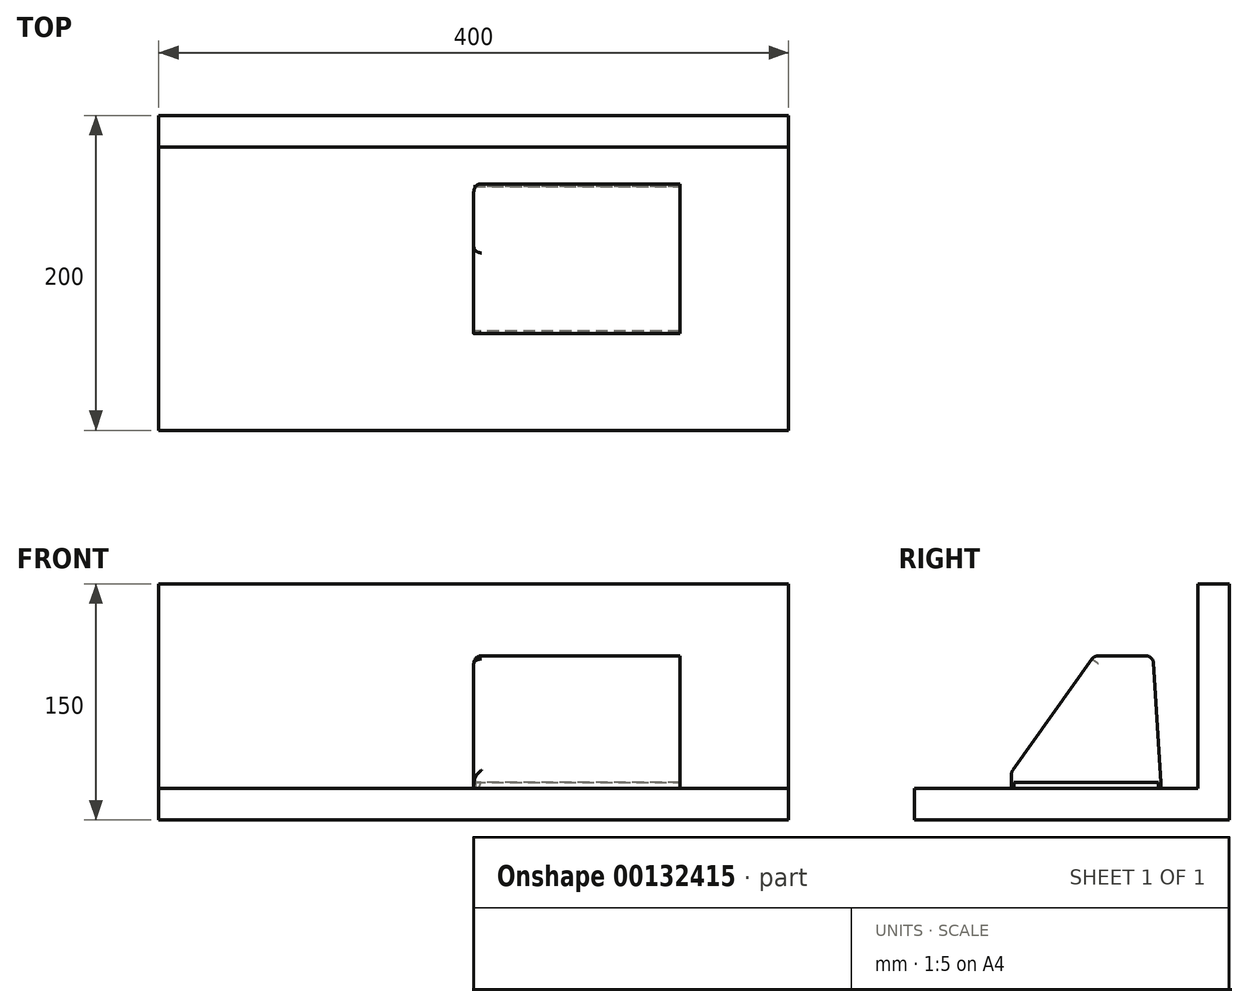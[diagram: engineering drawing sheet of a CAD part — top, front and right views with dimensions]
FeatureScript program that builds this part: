
annotation { "Feature Type Name" : "Feature", "Feature Type Description" : "" }
export const myFeature = defineFeature(function(context is Context, id is Id, definition is map)
    precondition{}
    {
        {
            var Q0;
            Q0=qCreatedBy(makeId("Right.planeOp"),FACE);
            var sketch = newSketch(context, id + "F0", { "sketchPlane" : qUnion([Q0])});
            skLineSegment(sketch, "E0", {"start": v(-180, 0) * mm, "end": v(0, 0) * mm});
            skLineSegment(sketch, "E1", {"start": v(0, 0) * mm, "end": v(0, 130) * mm});
            skLineSegment(sketch, "E2", {"start": v(0, 130) * mm, "end": v(20, 130) * mm});
            skLineSegment(sketch, "E3", {"start": v(20, 130) * mm, "end": v(20, -20) * mm});
            skLineSegment(sketch, "E4", {"start": v(20, -20) * mm, "end": v(-180, -20) * mm});
            skLineSegment(sketch, "E5", {"start": v(-180, -20) * mm, "end": v(-180, 0) * mm});
            skSolve(sketch);
        }
        {
            var Q0;
            Q0 = qSketchRegion(id + "F0", true);
            extrude(context, id + "F1", {"entities" : qUnion([Q0]), "endBound" : BoundingType.SYMMETRIC, "depth" : 400 * mm});
        }
        {
            var Q0;
            Q0=makeQuery(id+"F1.opExtrude","SWEPT_FACE",FACE,{"disambiguationData":[OSD([sQuery(id+"F0.wireOp",EDGE,"E0")])]});
            var sketch = newSketch(context, id + "F2", { "sketchPlane" : qUnion([Q0])});
            skLineSegment(sketch, "E6.bottom", {"start": v(0, -117) * mm, "end": v(131, -117) * mm});
            skLineSegment(sketch, "E6.top", {"start": v(0, -25) * mm, "end": v(131, -25) * mm});
            skLineSegment(sketch, "E6.left", {"start": v(0, -117) * mm, "end": v(0, -25) * mm});
            skLineSegment(sketch, "E6.right", {"start": v(131, -117) * mm, "end": v(131, -25) * mm});
            skSolve(sketch);
        }
        {
            var Q0;
            Q0 = qSketchRegion(id + "F2", true);
            extrude(context, id + "F3", {"entities" : qUnion([Q0]), "depth" : 4 * mm});
        }
        {
            var Q0;
            Q0=qCreatedBy(makeId("Right.planeOp"),FACE);
            var sketch = newSketch(context, id + "F4", { "sketchPlane" : qUnion([Q0])});
            skLineSegment(sketch, "E7", {"start": v(-65, 82.84) * mm, "end": v(-30, 82.84) * mm});
            skLineSegment(sketch, "E8", {"start": v(-25, 4) * mm, "end": v(-25, 0) * mm});
            skLineSegment(sketch, "E9.0", {"start": v(-23.5, 4.05) * mm, "end": v(-23.5, 0) * mm});
            skLineSegment(sketch, "E9.1", {"start": v(-118.5, 0) * mm, "end": v(-118.5, 10.48) * mm});
            skLineSegment(sketch, "E9.2", {"start": v(-118.5, 10.48) * mm, "end": v(-65.77, 84.34) * mm});
            skLineSegment(sketch, "E9.3", {"start": v(-65.77, 84.34) * mm, "end": v(-28.6, 84.34) * mm});
            skLineSegment(sketch, "E9.4", {"start": v(-23.5, 4.05) * mm, "end": v(-28.6, 84.34) * mm});
            skLineSegment(sketch, "E10", {"start": v(-117, 4) * mm, "end": v(-25, 4) * mm});
            skLineSegment(sketch, "E11", {"start": v(-117, 4) * mm, "end": v(-117, 0) * mm});
            skLineSegment(sketch, "E12", {"start": v(-118.5, 0) * mm, "end": v(-117, 0) * mm});
            skLineSegment(sketch, "E13", {"start": v(-25, 0) * mm, "end": v(-23.5, 0) * mm});
            skSolve(sketch);
        }
        {
            var Q0;
            Q0 = qSketchRegion(id + "F4", true);
            var Q1;
            Q1=makeQuery(id+"F3.opExtrude","SWEPT_FACE",FACE,{"disambiguationData":[OSD([sQuery(id+"F2.wireOp",EDGE,"E6.right")])]});
            extrude(context, id + "F5", {"entities" : qUnion([Q0]), "endBound" : BoundingType.UP_TO_SURFACE, "endBoundEntityFace" : qUnion([Q1]), "depth" : 124 * mm});
        }
        {
            var Q0;
            Q0=makeQuery(id+"F5.opExtrude","TWEAK_EDGE",EDGE,{"derivedFrom":[makeQuery(id+"F3.opExtrude","SWEPT_FACE",FACE,{"disambiguationData":[OSD([sQuery(id+"F2.wireOp",EDGE,"E6.right")])]}),makeQuery(id+"F4.imprint","IMPRINT",EDGE,{"derivedFrom":sQuery(id+"F4.wireOp",EDGE,"E9.2")})]});
            var Q1;
            Q1=makeQuery(id+"F5.opExtrude","CAP_EDGE",EDGE,{"disambiguationData":[OSD([sQuery(id+"F4.wireOp",EDGE,"E9.2")])],"isStart":true});
            var Q2;
            Q2=makeQuery(id+"F5.opExtrude","SWEPT_EDGE",EDGE,{"disambiguationData":[OSD([sQuery(id+"F4.wireOp",EDGE,"E9.1"),sQuery(id+"F4.wireOp",EDGE,"E9.2")])]});
            var Q3;
            Q3=makeQuery(id+"F5.opExtrude","SWEPT_EDGE",EDGE,{"disambiguationData":[OSD([sQuery(id+"F4.wireOp",EDGE,"E9.2"),sQuery(id+"F4.wireOp",EDGE,"E9.3")])]});
            fillet(context, id + "F6", {"entities" : qUnion([Q0, Q1, Q2, Q3]), "radius" : 5 * mm, "tangentPropagation" : true, "allowEdgeOverflow" : false});
        }
        {
            var Q0;
            Q0=makeQuery(id+"F5.opExtrude","TWEAK_EDGE",EDGE,{"derivedFrom":[makeQuery(id+"F3.opExtrude","SWEPT_FACE",FACE,{"disambiguationData":[OSD([sQuery(id+"F2.wireOp",EDGE,"E6.right")])]}),makeQuery(id+"F4.imprint","IMPRINT",EDGE,{"derivedFrom":sQuery(id+"F4.wireOp",EDGE,"E9.3")})]});
            var Q1;
            Q1=makeQuery(id+"F5.opExtrude","SWEPT_EDGE",EDGE,{"disambiguationData":[OSD([sQuery(id+"F4.wireOp",EDGE,"E9.3"),sQuery(id+"F4.wireOp",EDGE,"E9.4")])]});
            var Q2;
            Q2=makeQuery(id+"F5.opExtrude","CAP_EDGE",EDGE,{"disambiguationData":[OSD([sQuery(id+"F4.wireOp",EDGE,"E9.3")])],"isStart":true});
            var Q3;
            Q3=makeQuery(id+"F5.opExtrude","TWEAK_EDGE",EDGE,{"derivedFrom":[makeQuery(id+"F3.opExtrude","SWEPT_FACE",FACE,{"disambiguationData":[OSD([sQuery(id+"F2.wireOp",EDGE,"E6.right")])]}),makeQuery(id+"F4.imprint","IMPRINT",EDGE,{"derivedFrom":sQuery(id+"F4.wireOp",EDGE,"E9.4")})]});
            var Q4;
            Q4=makeQuery(id+"F5.opExtrude","CAP_EDGE",EDGE,{"disambiguationData":[OSD([sQuery(id+"F4.wireOp",EDGE,"E9.4")])],"isStart":true});
            fillet(context, id + "F7", {"entities" : qUnion([Q0, Q1, Q2, Q3, Q4]), "radius" : 5 * mm, "tangentPropagation" : true, "allowEdgeOverflow" : false});
        }
    });
